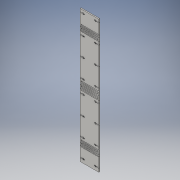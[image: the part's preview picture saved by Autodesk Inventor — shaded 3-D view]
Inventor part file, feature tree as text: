
AUTODESK INVENTOR PART (.ipt)
format: ipt  version: 2016 (Build 200138000, 138)  size: 465,920 bytes
history: native  units: in
note: dims shown in document units (in); Inventor stores cm internally (conversion verified against a paired STEP export)
features: extrude x1, sketch x1
ambient origin geometry x8: Origin, YZ Plane, XZ Plane, XY Plane, X Axis, Y Axis, Z Axis, Center Point
bodies: Solid1 (feature_tree)
feature tree (2):
  extrude  "Extrusion1"  Depth=0.1in
  sketch  "Sketch1"  dims[d34=0.427in d66=0.1in d94=2.7414in d95=2.7414in d109=0.305in d125=2.741in d127=0.6074in d128=0.6074in d130=0.6074in d162=0.942in d166=2.0in d167=2.0in d179=20.1074in d180=0.18in d181=0.0in d184=1.5in d188=1.5in d190=2.0in d191=0.9422in d192=2.84in d193=2.84in d194=2.84in d195=1.5in d197=0.1178in d198=0.1178in d199=0.1178in d200=2.2356in d201=1.5in d206=0.192in d207=2.84in d211=2.84in d212=2.84in d213=2.84in d214=2.84in d216=2.84in d217=2.84in d218=2.84in d219=2.84in d220=2.84in d221=2.84in d222=2.84in d223=0.427in d224=0.192in d228=2.84in d233=0.1in d234=0.1in d235=0.192in d236=0.1in d237=0.427in d238=0.192in d239=0.1in d240=0.427in d241=0.1923in d242=0.1004in d243=0.427in d244=0.1923in d245=0.1004in d246=0.427in d247=0.1004in d248=0.1923in d251=0.1004in d252=0.1923in d253=0.1923in d254=0.1004in d255=0.1923in d256=0.1004in d257=0.427in d258=0.1923in d259=0.1004in d260=0.427in d261=2.84in d262=0.1004in d263=0.1923in d264=0.1923in d265=0.427in d266=0.1in d267=0.192in d268=0.427in d269=0.192in d270=0.1in d271=0.427in d272=0.1in d273=0.192in d274=0.192in d275=0.1in d276=0.427in d277=0.192in d278=0.1in d279=0.427in d280=2.84in d281=2.84in d282=2.84in d283=2.84in d284=2.741in d285=2.741in d286=0.428in d287=0.062in d288=90.0deg d289=0.1in d290=0.192in d291=0.1in d292=0.062in]
